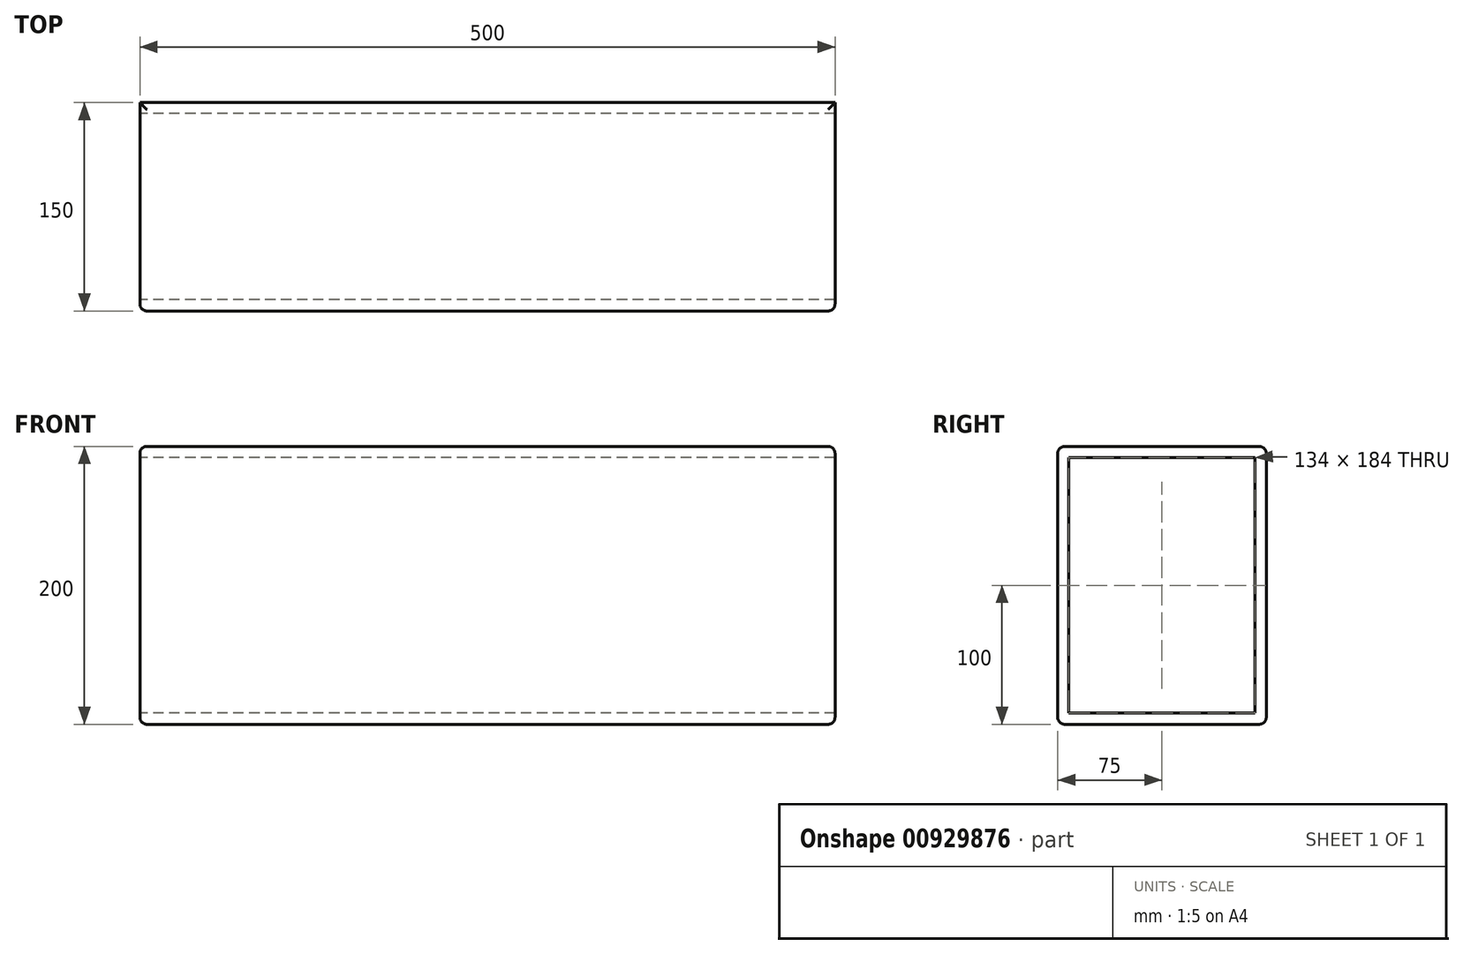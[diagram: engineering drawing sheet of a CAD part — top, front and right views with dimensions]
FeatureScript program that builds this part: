
annotation { "Feature Type Name" : "Feature", "Feature Type Description" : "" }
export const myFeature = defineFeature(function(context is Context, id is Id, definition is map)
    precondition{}
    {
        {
            var Q0;
            Q0=qCreatedBy(makeId("Front.planeOp"),FACE);
            var sketch = newSketch(context, id + "F0", { "sketchPlane" : qUnion([Q0])});
            skLineSegment(sketch, "E0.bottom", {"start": v(250, -100) * mm, "end": v(-250, -100) * mm});
            skLineSegment(sketch, "E0.top", {"start": v(250, 100) * mm, "end": v(-250, 100) * mm});
            skLineSegment(sketch, "E0.left", {"start": v(250, -100) * mm, "end": v(250, 100) * mm});
            skLineSegment(sketch, "E0.right", {"start": v(-250, -100) * mm, "end": v(-250, 100) * mm});
            skPoint(sketch, "E0.middle", {"position": v(0, 0) * mm});
            skLineSegment(sketch, "E1", {"start": v(-250, 0) * mm, "end": v(250, 0) * mm, "construction": true});
            skCircle(sketch, "E2", {"center": v(-70, 0) * mm, "radius": 14 * mm});
            skCircle(sketch, "E3", {"center": v(0, 0) * mm, "radius": 17 * mm});
            skCircle(sketch, "E4", {"center": v(80, 0) * mm, "radius": 26.5 * mm});
            skCircle(sketch, "E5.1.0.0", {"center": v(-140, 0) * mm, "radius": 14 * mm});
            skCircle(sketch, "E5.2.0.0", {"center": v(-210, 0) * mm, "radius": 14 * mm});
            skLineSegment(sketch, "E5.direction1", {"start": v(-70, 0) * mm, "end": v(-140, 0) * mm, "construction": true});
            skSolve(sketch);
        }
        {
            var Q0;
            Q0=makeQuery(id+"F0.imprint","IMPRINT",FACE,{"disambiguationData":[TD([[makeQuery(id+"F0.imprint","IMPRINT",EDGE,{"derivedFrom":sQuery(id+"F0.wireOp",EDGE,"E0.bottom")}),-1.0]])]});
            var Q1;
            Q1=makeQuery(id+"F0.imprint","IMPRINT",FACE,{"disambiguationData":[TD([[makeQuery(id+"F0.imprint","IMPRINT",EDGE,{"derivedFrom":sQuery(id+"F0.wireOp",EDGE,"E5.2.0.0")}),1.0]])]});
            var Q2;
            Q2=makeQuery(id+"F0.imprint","IMPRINT",FACE,{"disambiguationData":[TD([[makeQuery(id+"F0.imprint","IMPRINT",EDGE,{"derivedFrom":sQuery(id+"F0.wireOp",EDGE,"E5.1.0.0")}),1.0]])]});
            var Q3;
            Q3=makeQuery(id+"F0.imprint","IMPRINT",FACE,{"disambiguationData":[TD([[makeQuery(id+"F0.imprint","IMPRINT",EDGE,{"derivedFrom":sQuery(id+"F0.wireOp",EDGE,"E2")}),1.0]])]});
            var Q4;
            Q4=makeQuery(id+"F0.imprint","IMPRINT",FACE,{"disambiguationData":[TD([[makeQuery(id+"F0.imprint","IMPRINT",EDGE,{"derivedFrom":sQuery(id+"F0.wireOp",EDGE,"E3")}),1.0]])]});
            var Q5;
            Q5=makeQuery(id+"F0.imprint","IMPRINT",FACE,{"disambiguationData":[TD([[makeQuery(id+"F0.imprint","IMPRINT",EDGE,{"derivedFrom":sQuery(id+"F0.wireOp",EDGE,"E4")}),1.0]])]});
            extrude(context, id + "F1", {"entities" : qUnion([Q0, Q1, Q2, Q3, Q4, Q5]), "endBound" : BoundingType.SYMMETRIC, "depth" : 150 * mm, "offsetDistance" : 25 * mm});
        }
        {
            var Q0;
            Q0=makeQuery(id+"F1.opExtrude","SWEPT_FACE",FACE,{"disambiguationData":[OSD([sQuery(id+"F0.wireOp",EDGE,"E0.left")])]});
            var Q1;
            Q1=makeQuery(id+"F1.opExtrude","SWEPT_FACE",FACE,{"disambiguationData":[OSD([sQuery(id+"F0.wireOp",EDGE,"E0.right")])]});
            shell(context, id + "F2", {"entities" : qUnion([Q0, Q1]), "thickness" : 8 * mm});
        }
        {
            var Q0;
            Q0=makeQuery(id+"F1.opExtrude","CAP_EDGE",EDGE,{"disambiguationData":[OSD([sQuery(id+"F0.wireOp",EDGE,"E0.top")])],"isStart":true});
            var Q1;
            Q1=makeQuery(id+"F1.opExtrude","CAP_EDGE",EDGE,{"disambiguationData":[OSD([sQuery(id+"F0.wireOp",EDGE,"E0.bottom")])],"isStart":false});
            var Q2;
            Q2=makeQuery(id+"F1.opExtrude","CAP_FACE",FACE,{"disambiguationData":[OSD([sQuery(id+"F0.wireOp",EDGE,"E0.bottom"),sQuery(id+"F0.wireOp",EDGE,"E0.top"),sQuery(id+"F0.wireOp",EDGE,"E0.left"),sQuery(id+"F0.wireOp",EDGE,"E0.right")])],"isStart":false});
            var Q3;
            Q3=makeQuery(id+"F1.opExtrude","SWEPT_FACE",FACE,{"disambiguationData":[OSD([sQuery(id+"F0.wireOp",EDGE,"E0.top")])]});
            var Q4;
            Q4=makeQuery(id+"F1.opExtrude","CAP_EDGE",EDGE,{"disambiguationData":[OSD([sQuery(id+"F0.wireOp",EDGE,"E0.bottom")])],"isStart":true});
            var Q5;
            Q5=makeQuery(id+"F1.opExtrude","SWEPT_FACE",FACE,{"disambiguationData":[OSD([sQuery(id+"F0.wireOp",EDGE,"E0.bottom")])]});
            fillet(context, id + "F3", {"entities" : qUnion([Q0, Q1, Q2, Q3, Q4, Q5]), "radius" : 5 * mm, "tangentPropagation" : true, "allowEdgeOverflow" : false});
        }
    });
